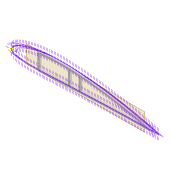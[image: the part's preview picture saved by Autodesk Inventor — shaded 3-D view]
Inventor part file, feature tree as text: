
AUTODESK INVENTOR PART (.ipt)
format: ipt  version: 2022 (Build 260153000, 153)  size: 355,840 bytes
history: native  units: mm
features: extrude x6, sketch x6, projected_geometry x5, shell x1, fillet x1, plane x1
ambient origin geometry x8: Origin, YZ Plane, XZ Plane, XY Plane, X Axis, Y Axis, Z Axis, Center Point
bodies: Solid1 (feature_tree)
feature tree (20):
  extrude  "Extrusion1"  Depth=4.8mm
  shell  "Shell1"  Thickness=2.0mm
  extrude  "Extrusion8"  Depth=5.9mm
  extrude  "Extrusion3"  Depth=10.0mm TaperAngle=0.0deg
  extrude  "Extrusion4"  Depth=2.0mm
  fillet  "Fillet1"  Radius=5.0mm
  extrude  "Extrusion5"  Depth=2.5mm
  plane  "Work Plane2"
  extrude  "Extrusion9"  Depth=0.5mm
  sketch  "Sketch3"  dims[d0=4.0mm d1=0.0mm d2=4.8mm d7=2.0mm]
  sketch  "Sketch8"  dims[d8=2.0mm d9=5.9mm]
  sketch  "Sketch9"  dims[d13=10.0mm d14=0.0mm d16=10.0mm d17=0.0mm]
  sketch  "Sketch10"  dims[d22=4.0mm d23=0.0mm d31=2.0mm d32=5.0mm]
  projected_geometry  "Projected Loop4"
  projected_geometry  "Projected Loop10"
  sketch  "Sketch24"  dims[d34=1.6mm d35=2.5mm]
  projected_geometry  "Projected Loop11"
  projected_geometry  "Projected Loop12"
  sketch  "Sketch25"  dims[d37=5.0mm d38=1.6mm d40=2.5mm d62=65.0mm d63=6.0mm d64=4.0mm d65=0.0mm d66=3.0mm d67=10.0mm d68=70.0mm d69=20.0mm d70=0.5mm d71=10.0mm d72=0.0mm]
  projected_geometry  "Projected Loop13"
